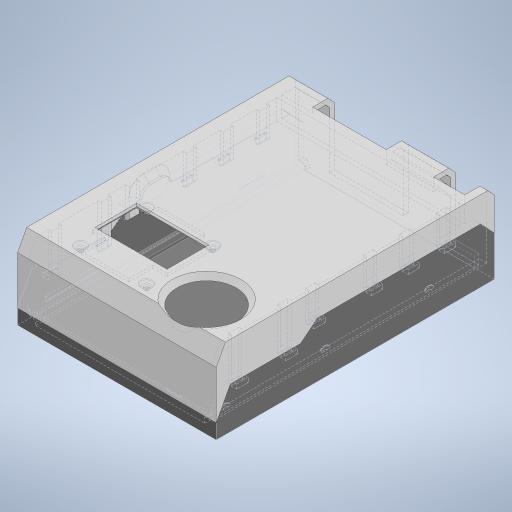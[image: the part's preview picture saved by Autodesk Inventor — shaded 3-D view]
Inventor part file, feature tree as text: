
AUTODESK INVENTOR PART (.ipt)
format: ipt  version: 2024.1 (Build 281209000, 209)  size: 1,723,904 bytes
history: native  units: mm
features: sketch x57, extrude x55, projected_geometry x38, chamfer x15, fillet x5, other x3, mirror x2, pattern_linear x1, plane x1
ambient origin geometry x8: Origin, YZ Plane, XZ Plane, XY Plane, X Axis, Y Axis, Z Axis, Center Point
bodies: Body1 (feature_tree), Body2 (feature_tree), Body3 (feature_tree)
feature tree (177):
  other  "pcb"
  extrude  "Extrusion1"  Depth=95.0mm
  chamfer  "Chamfer1"  Distance=1.57mm
  extrude  "Extrusion2"  Depth=10.8mm
  chamfer  "Chamfer2"  Distance=10.12mm
  chamfer  "Chamfer19"  Distance=3.0mm Angle=45.0deg
  chamfer  "Chamfer20"  Distance=15.0mm
  extrude  "Extrusion3"  Depth=1.2mm
  extrude  "Extrusion5"  Depth=17.9mm
  extrude  "Extrusion6"  Depth=2.44mm
  extrude  "Extrusion7"  Depth=1.63mm TaperAngle=0.0deg
  fillet  "Fillet1"  Radius=0.1mm
  fillet  "Fillet2"  Radius=5.0mm
  extrude  "Extrusion14"  Depth=5.0mm
  extrude  "Extrusion8"  Depth=3.2mm TaperAngle=0.0deg
  extrude  "Extrusion9"  Depth=3.0mm
  extrude  "Extrusion10"  Depth=2.37mm
  sketch  "Sketch12"  dims[d21=30.0mm d22=15.0mm d23=0.0mm]
  extrude  "Extrusion11"  Depth=10.2mm
  extrude  "Extrusion12"  Depth=9.0mm
  fillet  "Fillet3"  Radius=0.1mm
  extrude  "Extrusion13"  Depth=25.94mm
  extrude  "Extrusion88"  Depth=0.56mm
  extrude  "Extrusion89"  Depth=4.0mm
  fillet  "Fillet10"  Radius=16.58mm
  extrude  "Extrusion90"  Depth=0.1mm
  extrude  "Extrusion23"  Depth=0.1mm
  chamfer  "Chamfer3"  Distance=0.2mm
  pattern_linear  "Rectangular Pattern1"  Count1=2 Spacing1=55.0mm
  extrude  "CASE - START"  Depth=2.0mm
  extrude  "Extrusion25"  Depth=3.0mm
  extrude  "Extrusion26"  Depth=1.64mm
  chamfer  "Chamfer4"  Distance=1.64mm
  extrude  "Extrusion27"  Depth=20.0mm
  extrude  "Extrusion28"  Depth=8.0mm
  extrude  "Extrusion29"  Depth=1.64mm TaperAngle=45.0deg
  chamfer  "Chamfer5"  Distance=1.64mm
  fillet  "Fillet7"  Radius=2.2mm
  extrude  "Extrusion30"  Depth=0.5mm
  chamfer  "Chamfer6"  Distance=1.64mm
  extrude  "Extrusion33"  Depth=0.5mm
  extrude  "Extrusion35"  Depth=0.5mm
  chamfer  "Chamfer7"  Distance=5.0mm
  extrude  "Extrusion39"  Depth=0.5mm
  extrude  "Extrusion75"  Depth=0.5mm TaperAngle=0.0deg
  chamfer  "Chamfer9"  Distance=2.0mm Angle=45.0deg
  extrude  "Extrusion79"  Depth=0.5mm
  extrude  "Extrusion80"  TaperAngle=0.0deg  [1 undecoded]
  extrude  "Extrusion81"  Depth=0.5mm
  extrude  "Extrusion91"  Depth=10.0mm
  extrude  "Extrusion83"  Depth=0.5mm
  extrude  "Extrusion53"  [1 undecoded]
  extrude  "Extrusion92"  Depth=0.5mm
  extrude  "base-slots"  Depth=0.5mm
  extrude  "Extrusion62"  Depth=0.5mm
  extrude  "Extrusion63"  Depth=0.5mm
  extrude  "Extrusion64"  Depth=0.5mm TaperAngle=0.0deg
  extrude  "Extrusion65"  Depth=0.5mm TaperAngle=45.0deg
  extrude  "Extrusion66"  Depth=1.5mm TaperAngle=0.0deg
  sketch  "Sketch78"  dims[d81=23.5mm]
  extrude  "Extrusion93"  Depth=0.5mm TaperAngle=0.0deg
  extrude  "Extrusion94"  Depth=0.5mm TaperAngle=45.0deg
  extrude  "Extrusion68"  Depth=0.5mm TaperAngle=0.0deg
  extrude  "Extrusion69"  Depth=0.5mm TaperAngle=45.0deg
  extrude  "Extrusion70"  Depth=10.0mm TaperAngle=0.0deg
  extrude  "Extrusion71"  Depth=1.5mm
  extrude  "Extrusion95"  Depth=0.5mm
  extrude  "Extrusion96"  Depth=0.5mm
  plane  "Work Plane1"
  chamfer  "Chamfer13"  Distance=4.0mm
  mirror  "Mirror1"
  mirror  "Mirror2"
  extrude  "Extrusion85"  Depth=0.5mm
  extrude  "Extrusion86"  Depth=0.5mm
  chamfer  "Chamfer15"  Distance=4.0mm
  chamfer  "Chamfer16"  Distance=4.0mm
  extrude  "Extrusion97"  Depth=0.5mm
  chamfer  "Chamfer21"  Distance=1.5mm
  chamfer  "Chamfer22"  Distance=2.0mm
  extrude  "Extrusion98"  Depth=0.5mm
  sketch  "Sketch110"  dims[d165=1.64mm d166=0.0mm d167=1.0mm d168=4.0mm d169=45.0deg]
  extrude  "Extrusion99"  Depth=0.5mm
  extrude  "Extrusion100"  TaperAngle=0.0deg  [1 undecoded]
  sketch  "Sketch1"  dims[d0=64.4mm d1=95.0mm]
  sketch  "Sketch2"  dims[d2=47.5mm]
  sketch  "Sketch3"  dims[d3=32.2mm d4=1.57mm d5=0.0mm]
  sketch  "Sketch5"  dims[d6=2.0mm d7=2.0mm d8=45.0deg d9=10.8mm]
  sketch  "Sketch7"  dims[d10=8.8mm]
  sketch  "Sketch8"  dims[d12=8.2mm d13=10.12mm d14=0.0mm d15=3.0mm d16=6.0mm d17=45.0deg]
  sketch  "Sketch9"  dims[d18=12.0mm]
  sketch  "Sketch10"  dims[d19=20.0mm]
  sketch  "Sketch11"  dims[d20=6.26mm]
  sketch  "Sketch13"  dims[d30=41.24mm d31=1.2mm]
  sketch  "Sketch14"  dims[d32=44.25mm d33=17.9mm]
  sketch  "Sketch15"  dims[d34=2.44mm d36=2.44mm]
  sketch  "Sketch17"  dims[d37=11.2mm d38=0.0mm d39=1.63mm d40=0.0mm d41=0.1mm d42=5.0mm]
  sketch  "Sketch26"  dims[d43=1.3mm d44=5.0mm]
  sketch  "Sketch28"  dims[d45=5.0mm d46=3.2mm d47=0.0mm]
  other  "case-bottom"
  sketch  "Sketch29"  dims[d48=2.0mm d49=3.0mm]
  projected_geometry  "Projected Loop2"
  sketch  "Sketch30"  dims[d50=4.0mm d51=2.37mm]
  sketch  "Sketch32"  dims[d52=17.0mm d53=10.2mm]
  sketch  "Sketch33"  dims[d54=10.9mm d55=0.0mm d56=9.0mm d57=0.1mm]
  sketch  "Sketch34"  dims[d58=26.0mm d59=25.94mm]
  projected_geometry  "Projected Loop3"
  sketch  "Sketch35"  dims[d60=1.06mm d61=0.0mm d62=0.56mm]
  projected_geometry  "Projected Loop4"
  projected_geometry  "Projected Loop5"
  sketch  "Sketch38"  dims[d63=0.56mm d64=4.0mm d65=16.58mm]
  sketch  "Sketch39"  dims[d66=1.3mm d67=0.0mm d68=0.1mm]
  projected_geometry  "Projected Loop9"
  projected_geometry  "Projected Loop11"
  other  "lid-1"
  sketch  "Sketch46"  dims[d69=0.1mm d70=0.1mm]
  projected_geometry  "Projected Loop14"
  projected_geometry  "Projected Loop15"
  projected_geometry  "Projected Loop16"
  projected_geometry  "Projected Loop17"
  projected_geometry  "Projected Loop18"
  projected_geometry  "Projected Loop19"
  sketch  "Sketch61"  dims[d71=14.0mm d72=0.2mm d73=0.0mm]
  sketch  "Sketch70"  dims[d74=7.0mm]
  sketch  "Sketch71"  dims[d75=7.0mm]
  sketch  "Sketch72"  dims[d76=0.2mm]
  sketch  "Sketch73"  dims[d77=0.2mm]
  sketch  "Sketch74"  dims[d78=0.2mm d79=0.0mm]
  sketch  "Sketch75"  dims[d80=2.0mm]
  projected_geometry  "Projected Loop52"
  sketch  "Sketch79"  dims[d82=23.5mm]
  projected_geometry  "Projected Loop54"
  sketch  "Sketch80"  dims[d83=1.9mm]
  sketch  "Sketch81"  dims[d84=1.22mm]
  sketch  "Sketch85"  dims[d85=1.22mm]
  sketch  "Sketch89"  dims[d86=1.25mm]
  sketch  "Sketch90"  dims[d87=1.25mm]
  projected_geometry  "Projected Loop68"
  projected_geometry  "Projected Loop69"
  sketch  "Sketch91"  dims[d88=0.0mm d89=0.0mm]
  sketch  "Sketch93"  dims[d90=3.6mm]
  projected_geometry  "Projected Loop75"
  sketch  "Sketch95"  dims[d91=3.6mm]
  projected_geometry  "Projected Loop76"
  sketch  "Sketch96"  dims[d92=15.5mm]
  projected_geometry  "Projected Loop77"
  projected_geometry  "Projected Loop78"
  projected_geometry  "Projected Loop79"
  projected_geometry  "Projected Loop80"
  sketch  "Sketch98"  dims[d93=0.1mm]
  sketch  "Sketch100"  dims[d94=3.8mm d95=0.0mm]
  sketch  "Sketch101"  dims[d139=5.31mm]
  projected_geometry  "Projected Loop82"
  projected_geometry  "Projected Loop83"
  projected_geometry  "Projected Loop84"
  projected_geometry  "Projected Loop85"
  sketch  "Sketch102"  dims[d140=5.31mm]
  projected_geometry  "Projected Loop86"
  projected_geometry  "Projected Loop87"
  projected_geometry  "Projected Loop88"
  projected_geometry  "Projected Loop89"
  sketch  "Sketch103"  dims[d141=1.37mm d142=0.0mm]
  projected_geometry  "Projected Loop90"
  sketch  "Sketch104"  dims[d143=1.0mm d144=4.0mm d145=45.0deg d146=20.0mm d148=55.0mm d149=20.0mm d151=87.0mm]
  projected_geometry  "Projected Loop91"
  sketch  "Sketch105"  dims[d152=2.0mm d153=2.0mm]
  projected_geometry  "Projected Loop92"
  sketch  "Sketch106"  dims[d154=2.0mm d155=3.0mm]
  projected_geometry  "Projected Loop93"
  sketch  "Sketch107"  dims[d156=2.0mm d157=0.0mm d158=0.2mm d159=1.64mm d160=0.0mm]
  projected_geometry  "Projected Loop94"
  sketch  "Sketch108"  dims[d161=5.0mm d162=20.0mm]
  sketch  "Sketch109"  dims[d163=13.0mm d164=8.0mm]
  projected_geometry  "Projected Loop95"
  sketch  "Sketch111"  dims[d171=1.5mm]
  projected_geometry  "Projected Loop96"
  sketch  "Sketch112"  dims[d172=3.3mm d173=1.64mm d174=0.0mm d175=2.2mm d176=0.5mm d177=1.64mm d178=0.0mm d180=5.0mm d181=5.0mm d182=5.0mm d183=0.8mm d184=2.0mm d185=0.0mm d186=2.0mm d187=4.0mm d188=45.0deg d189=0.5mm d191=0.0mm d192=9.0mm d194=10.0mm d195=9.445mm d196=-2.445mm d197=5.0mm d198=30.0mm d199=1.2mm d200=1.7mm d201=2.0mm d202=0.0mm d203=2.0mm d204=4.0mm d205=45.0deg d213=1.5mm d214=0.0mm d221=3.0mm d222=0.0mm d223=2.0mm d224=4.0mm d225=45.0deg d245=40.0mm d246=0.0mm d249=0.5mm d250=2.0mm d251=45.0deg d297=10.0mm d298=0.0mm d327=1.5mm d328=2.0mm d330=4.0mm d332=4.0mm d333=2.0mm d334=4.0mm d335=4.0mm d336=4.0mm d339=2.0mm d340=1.5mm d341=2.0mm d342=0.0mm d343=0.2mm d344=0.2mm d345=0.0mm d346=0.0mm d347=0.2mm d348=0.2mm d349=0.0mm d350=0.2mm d351=0.2mm d352=0.2mm d353=0.2mm d354=1.1mm d355=0.0mm d356=1.0mm d357=1.0mm d358=1.1mm d359=0.0mm d360=10.0mm d361=0.0mm d362=1.0mm d363=1.0mm d364=10.0mm d365=0.0mm d366=10.0mm d367=0.0mm d372=0.6mm d373=2.0mm d374=45.0deg d376=1.47mm d377=0.2mm d378=0.64mm d379=1.5mm d380=0.0mm d381=10.0mm d382=0.0mm d383=0.2mm d384=1.47mm d385=0.64mm d386=10.0mm d387=0.0mm d388=10.0mm d389=0.0mm d390=0.59mm d405=9.0mm d406=8.0mm d410=8.0mm d411=1.7mm d413=40.0mm d414=0.0mm d425=10.0mm d426=0.0mm d428=1.7mm d429=3.0mm d430=0.0mm d431=10.0mm d432=0.0mm d436=10.0mm d437=0.0mm d438=0.39mm d439=3.11mm d452=0.1mm d453=1.7mm d454=1.7mm d455=4.0mm d456=0.0mm d457=4.0mm d458=1.0mm d459=0.0mm d460=0.55mm d461=2.0mm d462=45.0deg d463=0.55mm d464=2.0mm d465=45.0deg d474=10.52mm d475=10.52mm d476=10.52mm d477=0.01mm d478=5.17mm d479=3.0mm d480=6.0mm d481=45.0deg d482=3.0mm d483=6.0mm d484=45.0deg d485=9.4mm d486=13.2mm d487=11.07mm d488=21.5mm d489=0.0mm d490=23.7mm d491=20.42mm d492=12.82mm d493=11.7mm d494=0.0mm d495=8.0mm d496=3.2mm d497=0.7mm d498=11.0mm d499=4.4mm d500=0.0mm d501=25.0mm d502=8.201332mm d503=8.201332mm d504=1.0mm d505=0.5mm d506=1.7mm d507=1.7mm d508=1.7mm d509=1.7mm d510=10.0mm d511=0.0mm d514=20.5mm d515=8.726646mm d516=1.7mm d517=10.0mm d518=0.0mm d519=4.0mm d520=4.0mm d521=9.0mm d522=9.0mm d523=0.2mm d524=0.2mm d525=0.2mm d526=0.2mm d527=1.1mm d528=0.0mm d529=10.0mm d530=0.0mm d531=10.0mm d532=0.0mm d533=10.0mm d534=0.0mm d535=1.0mm d536=0.0mm d537=2.0mm d538=2.0mm d539=45.0deg d540=3.0mm d541=2.0mm d542=45.0deg d543=1.0mm d544=0.0mm d545=0.75mm d546=0.5mm d547=0.0mm d548=0.5mm d549=0.0mm d247=0.5mm d248=0.872665mm d296=0.5mm d299=0.872665mm d433=0.5mm d434=0.872665mm]
  projected_geometry  "Projected Loop97"
note: 3 required parameter values undecoded (feature->parameter linkage not recoverable at this tier; creation-order binding heuristic only, values carry confidence <= 0.55)
